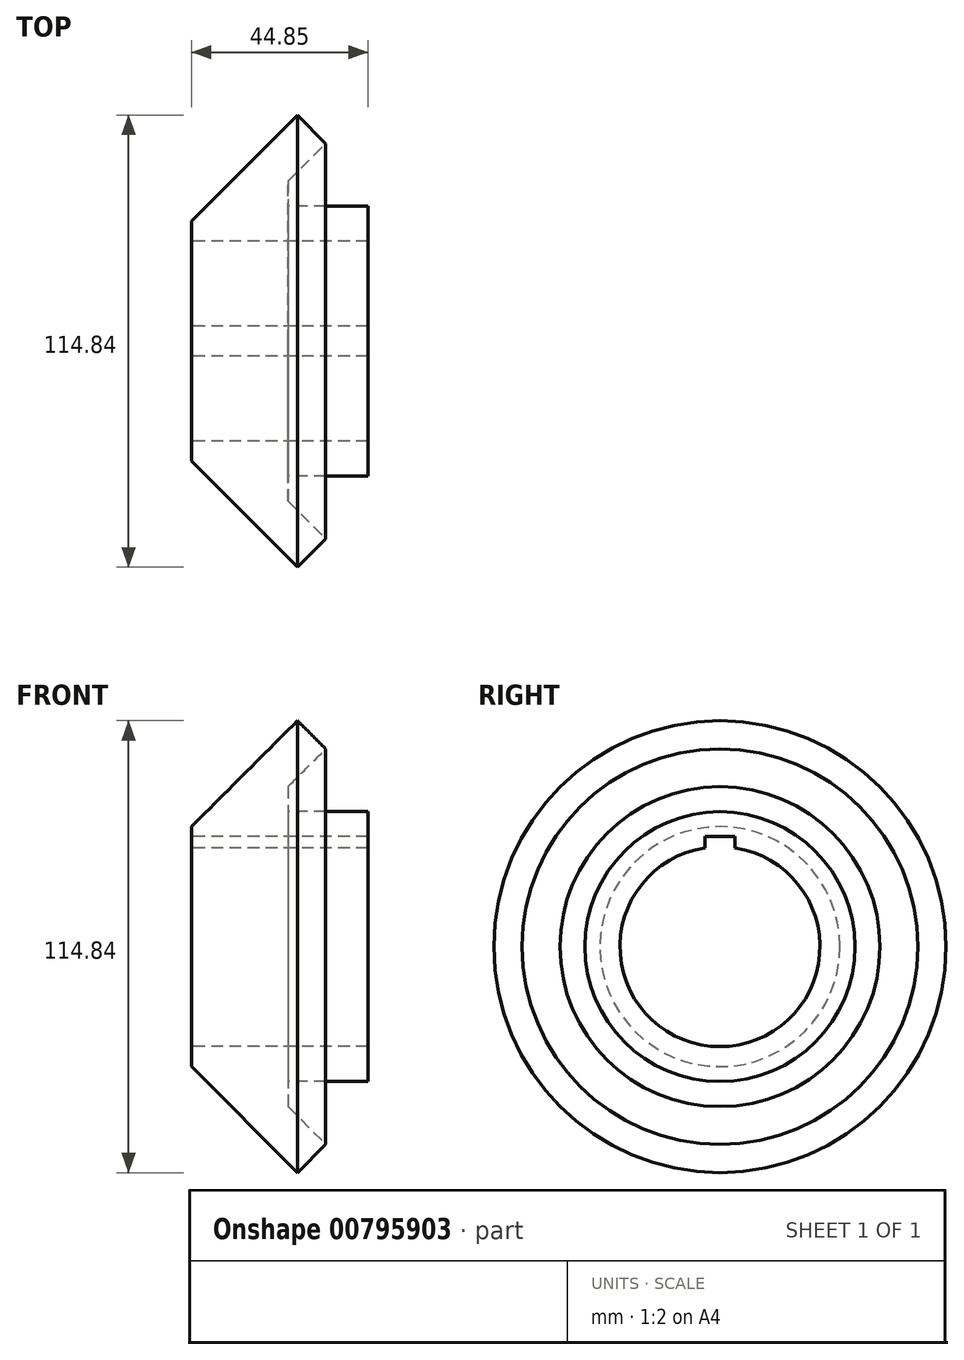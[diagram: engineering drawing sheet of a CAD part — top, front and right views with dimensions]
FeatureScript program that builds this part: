
annotation { "Feature Type Name" : "Feature", "Feature Type Description" : "" }
export const myFeature = defineFeature(function(context is Context, id is Id, definition is map)
    precondition{}
    {
        {
            var Q0;
            Q0=qCreatedBy(makeId("Top.planeOp"),FACE);
            var sketch = newSketch(context, id + "F0", { "sketchPlane" : qUnion([Q0])});
            skLineSegment(sketch, "E0", {"start": v(0, 0) * mm, "end": v(79.66, 79.66) * mm, "construction": true});
            skLineSegment(sketch, "E1", {"start": v(-68.41, 0) * mm, "end": v(72.2, 0) * mm, "construction": true});
            skLineSegment(sketch, "E2", {"start": v(0, 56.92) * mm, "end": v(0, -50.3) * mm, "construction": true});
            skLineSegment(sketch, "E3", {"start": v(75.33, 34.3) * mm, "end": v(55, 34.3) * mm});
            skLineSegment(sketch, "E4", {"start": v(55, 34.3) * mm, "end": v(55, 40.64) * mm});
            skLineSegment(sketch, "E5", {"start": v(55, 40.64) * mm, "end": v(64.6, 50.24) * mm});
            skLineSegment(sketch, "E6", {"start": v(64.6, 50.24) * mm, "end": v(57.42, 57.42) * mm});
            skLineSegment(sketch, "E7", {"start": v(75.33, 34.3) * mm, "end": v(75.33, 25.4) * mm});
            skLineSegment(sketch, "E8", {"start": v(75.33, 25.4) * mm, "end": v(30.48, 25.4) * mm});
            skLineSegment(sketch, "E9", {"start": v(30.48, 25.4) * mm, "end": v(30.48, 30.48) * mm});
            skLineSegment(sketch, "E10", {"start": v(30.48, 30.48) * mm, "end": v(57.42, 57.42) * mm});
            skSolve(sketch);
        }
        {
            var Q0;
            Q0=makeQuery(id+"F0.imprint","IMPRINT",FACE,{"disambiguationData":[TD([[makeQuery(id+"F0.imprint","IMPRINT",EDGE,{"derivedFrom":sQuery(id+"F0.wireOp",EDGE,"E3")}),1.0]])]});
            var Q1;
            Q1=sQuery(id+"F0.wireOp",EDGE,"E1");
            revolve(context, id + "F1", {"surfaceOperationType" : NewSurfaceOperationType.NEW, "entities" : qUnion([Q0]), "axis" : qUnion([Q1]), "revolveType" : RevolveType.FULL});
        }
        {
            var Q0;
            Q0=qCreatedBy(makeId("Right.planeOp"),FACE);
            var sketch = newSketch(context, id + "F2", { "sketchPlane" : qUnion([Q0])});
            skCircle(sketch, "E11", {"center": v(0, 0) * mm, "radius": 25.4 * mm});
            skLineSegment(sketch, "E12.bottom", {"start": v(3.81, 27.94) * mm, "end": v(-3.8, 27.94) * mm});
            skLineSegment(sketch, "E12.left", {"start": v(3.81, 27.94) * mm, "end": v(3.81, 25.11) * mm});
            skLineSegment(sketch, "E12.right", {"start": v(-3.8, 27.94) * mm, "end": v(-3.8, 25.11) * mm});
            skPoint(sketch, "E12.middle", {"position": v(0, 25.4) * mm});
            skPoint(sketch, "E13.orphan", {"position": v(3.81, 22.86) * mm});
            skPoint(sketch, "E14.orphan", {"position": v(-3.8, 22.86) * mm});
            skSolve(sketch);
        }
        {
            var Q0;
            Q0=makeQuery(id+"F2.imprint","IMPRINT",FACE,{"disambiguationData":[TD([[makeQuery(id+"F2.imprint","IMPRINT",EDGE,{"derivedFrom":sQuery(id+"F2.wireOp",EDGE,"E12.bottom")}),1.0]])]});
            var Q1;
            Q1=makeQuery(id+"F1.opRevolve","SWEPT_FACE",FACE,{"disambiguationData":[OSD([sQuery(id+"F0.wireOp",EDGE,"E7")])]});
            extrude(context, id + "F3", {"entities" : qUnion([Q0]), "operationType" : NewBodyOperationType.REMOVE, "endBound" : BoundingType.UP_TO_SURFACE, "depth" : 25.4 * mm, "endBoundEntityFace" : qUnion([Q1]), "offsetDistance" : 25.4 * mm});
        }
    });
